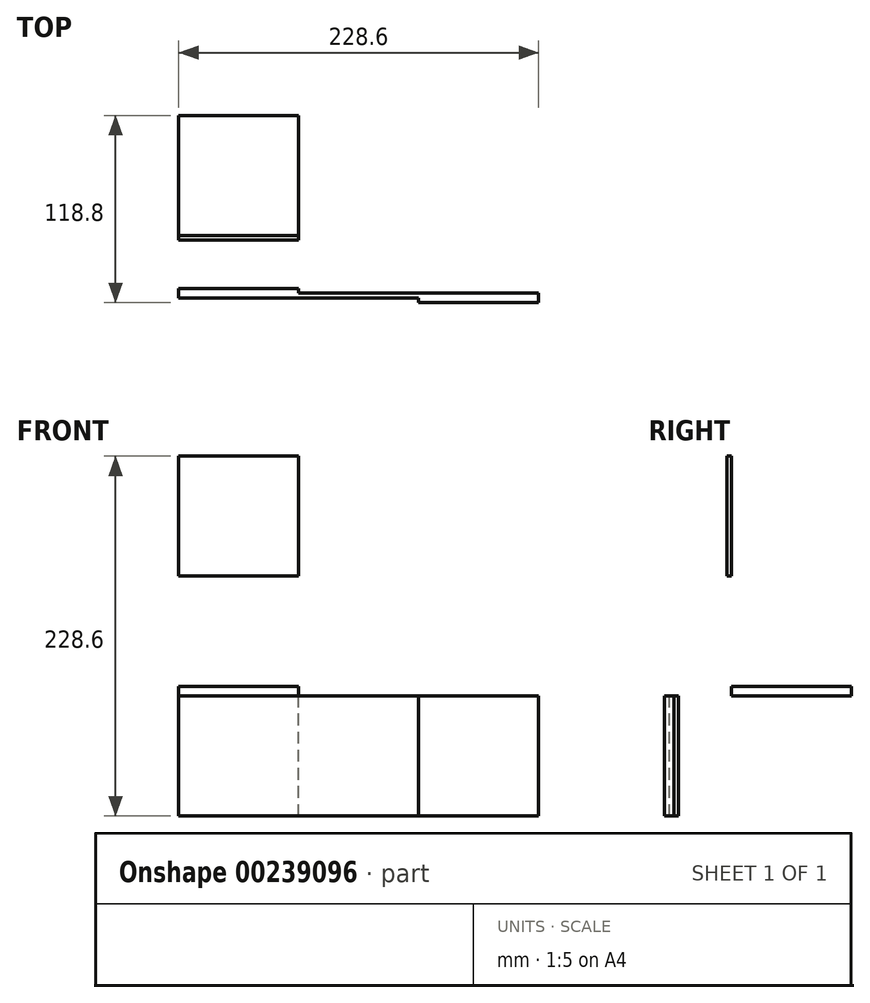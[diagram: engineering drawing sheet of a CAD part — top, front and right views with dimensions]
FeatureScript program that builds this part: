
annotation { "Feature Type Name" : "Feature", "Feature Type Description" : "" }
export const myFeature = defineFeature(function(context is Context, id is Id, definition is map)
    precondition{}
    {
        {
            assignVariable(context, id + "F0", {"name" : "v", "anyValue" : 3});
        }
        {
            var Q0;
            Q0=qCreatedBy(makeId("Front.planeOp"),FACE);
            var sketch = newSketch(context, id + "F1", { "sketchPlane" : qUnion([Q0])});
            skLineSegment(sketch, "E0.bottom", {"start": v(-114.3, 38.1) * mm, "end": v(114.3, 38.1) * mm});
            skLineSegment(sketch, "E0.top", {"start": v(-114.3, -38.1) * mm, "end": v(114.3, -38.1) * mm});
            skLineSegment(sketch, "E0.left", {"start": v(-114.3, 38.1) * mm, "end": v(-114.3, -38.1) * mm});
            skLineSegment(sketch, "E0.right", {"start": v(114.3, 38.1) * mm, "end": v(114.3, -38.1) * mm});
            skPoint(sketch, "E0.middle", {"position": v(0, 0) * mm});
            skSolve(sketch);
        }
        {
            var Q0;
            Q0 = qSketchRegion(id + "F1", true);
            extrude(context, id + "F2", {"entities" : qUnion([Q0]), "endBound" : BoundingType.SYMMETRIC, "depth" : (getVariable(context, 'v')) * mm});
        }
        {
            var Q0;
            Q0=makeQuery(id+"F2.opExtrude","CAP_FACE",FACE,{"disambiguationData":[OSD([sQuery(id+"F1.wireOp",EDGE,"E0.bottom"),sQuery(id+"F1.wireOp",EDGE,"E0.top"),sQuery(id+"F1.wireOp",EDGE,"E0.left"),sQuery(id+"F1.wireOp",EDGE,"E0.right")])],"isStart":false});
            var sketch = newSketch(context, id + "F3", { "sketchPlane" : qUnion([Q0])});
            skLineSegment(sketch, "E1.bottom", {"start": v(114.3, -38.1) * mm, "end": v(38.1, -38.1) * mm});
            skLineSegment(sketch, "E1.top", {"start": v(114.3, 38.1) * mm, "end": v(38.1, 38.1) * mm});
            skLineSegment(sketch, "E1.left", {"start": v(114.3, -38.1) * mm, "end": v(114.3, 38.1) * mm});
            skLineSegment(sketch, "E1.right", {"start": v(38.1, -38.1) * mm, "end": v(38.1, 38.1) * mm});
            skSolve(sketch);
        }
        {
            var Q0;
            Q0 = qSketchRegion(id + "F3", true);
            extrude(context, id + "F4", {"entities" : qUnion([Q0]), "operationType" : NewBodyOperationType.ADD, "depth" : (getVariable(context, 'v')) * mm});
        }
        {
            var Q0;
            Q0=makeQuery(id+"F2.opExtrude","CAP_FACE",FACE,{"disambiguationData":[OSD([sQuery(id+"F1.wireOp",EDGE,"E0.bottom"),sQuery(id+"F1.wireOp",EDGE,"E0.top"),sQuery(id+"F1.wireOp",EDGE,"E0.left"),sQuery(id+"F1.wireOp",EDGE,"E0.right")])],"isStart":true});
            var sketch = newSketch(context, id + "F5", { "sketchPlane" : qUnion([Q0])});
            skLineSegment(sketch, "E2.bottom", {"start": v(114.3, -38.1) * mm, "end": v(38.1, -38.1) * mm});
            skLineSegment(sketch, "E2.top", {"start": v(114.3, 38.1) * mm, "end": v(38.1, 38.1) * mm});
            skLineSegment(sketch, "E2.left", {"start": v(114.3, -38.1) * mm, "end": v(114.3, 38.1) * mm});
            skLineSegment(sketch, "E2.right", {"start": v(38.1, -38.1) * mm, "end": v(38.1, 38.1) * mm});
            skSolve(sketch);
        }
        {
            var Q0;
            Q0 = qSketchRegion(id + "F5", true);
            extrude(context, id + "F6", {"entities" : qUnion([Q0]), "operationType" : NewBodyOperationType.ADD, "depth" : (getVariable(context, 'v')) * mm});
        }
        {
            var Q0;
            Q0=makeQuery(id+"F6.boolean.opBoolean","MERGE",FACE,{"derivedFrom":[makeQuery(id+"F4.boolean.opBoolean","MERGE",FACE,{"derivedFrom":[makeQuery(id+"F2.opExtrude","SWEPT_FACE",FACE,{"disambiguationData":[OSD([sQuery(id+"F1.wireOp",EDGE,"E0.bottom")])]}),makeQuery(id+"F4.opExtrude","SWEPT_FACE",FACE,{"disambiguationData":[OSD([sQuery(id+"F3.wireOp",EDGE,"E1.top")])]})]}),makeQuery(id+"F6.opExtrude","SWEPT_FACE",FACE,{"disambiguationData":[OSD([sQuery(id+"F5.wireOp",EDGE,"E2.top")])]})]});
            var sketch = newSketch(context, id + "F7", { "sketchPlane" : qUnion([Q0])});
            skLineSegment(sketch, "E3.bottom", {"start": v(-38.1, 114.3) * mm, "end": v(-114.3, 114.3) * mm});
            skLineSegment(sketch, "E3.top", {"start": v(-38.1, 38.1) * mm, "end": v(-114.3, 38.1) * mm});
            skLineSegment(sketch, "E3.left", {"start": v(-38.1, 114.3) * mm, "end": v(-38.1, 38.1) * mm});
            skLineSegment(sketch, "E3.right", {"start": v(-114.3, 114.3) * mm, "end": v(-114.3, 38.1) * mm});
            skSolve(sketch);
        }
        {
            var Q0;
            Q0 = qSketchRegion(id + "F7", true);
            extrude(context, id + "F8", {"entities" : qUnion([Q0]), "operationType" : NewBodyOperationType.ADD, "depth" : (2 * getVariable(context, 'v')) * mm});
        }
        {
            var Q0;
            Q0=makeQuery(id+"F8.opExtrude","SWEPT_FACE",FACE,{"disambiguationData":[OSD([sQuery(id+"F7.wireOp",EDGE,"E3.top")])]});
            var sketch = newSketch(context, id + "F9", { "sketchPlane" : qUnion([Q0])});
            skLineSegment(sketch, "E4.bottom", {"start": v(-114.3, 190.5) * mm, "end": v(-38.1, 190.5) * mm});
            skLineSegment(sketch, "E4.top", {"start": v(-114.3, 114.3) * mm, "end": v(-38.1, 114.3) * mm});
            skLineSegment(sketch, "E4.left", {"start": v(-114.3, 190.5) * mm, "end": v(-114.3, 114.3) * mm});
            skLineSegment(sketch, "E4.right", {"start": v(-38.1, 190.5) * mm, "end": v(-38.1, 114.3) * mm});
            skSolve(sketch);
        }
        {
            var Q0;
            Q0 = qSketchRegion(id + "F9", true);
            extrude(context, id + "F10", {"entities" : qUnion([Q0]), "operationType" : NewBodyOperationType.ADD, "depth" : (getVariable(context, 'v')) * mm});
        }
    });
